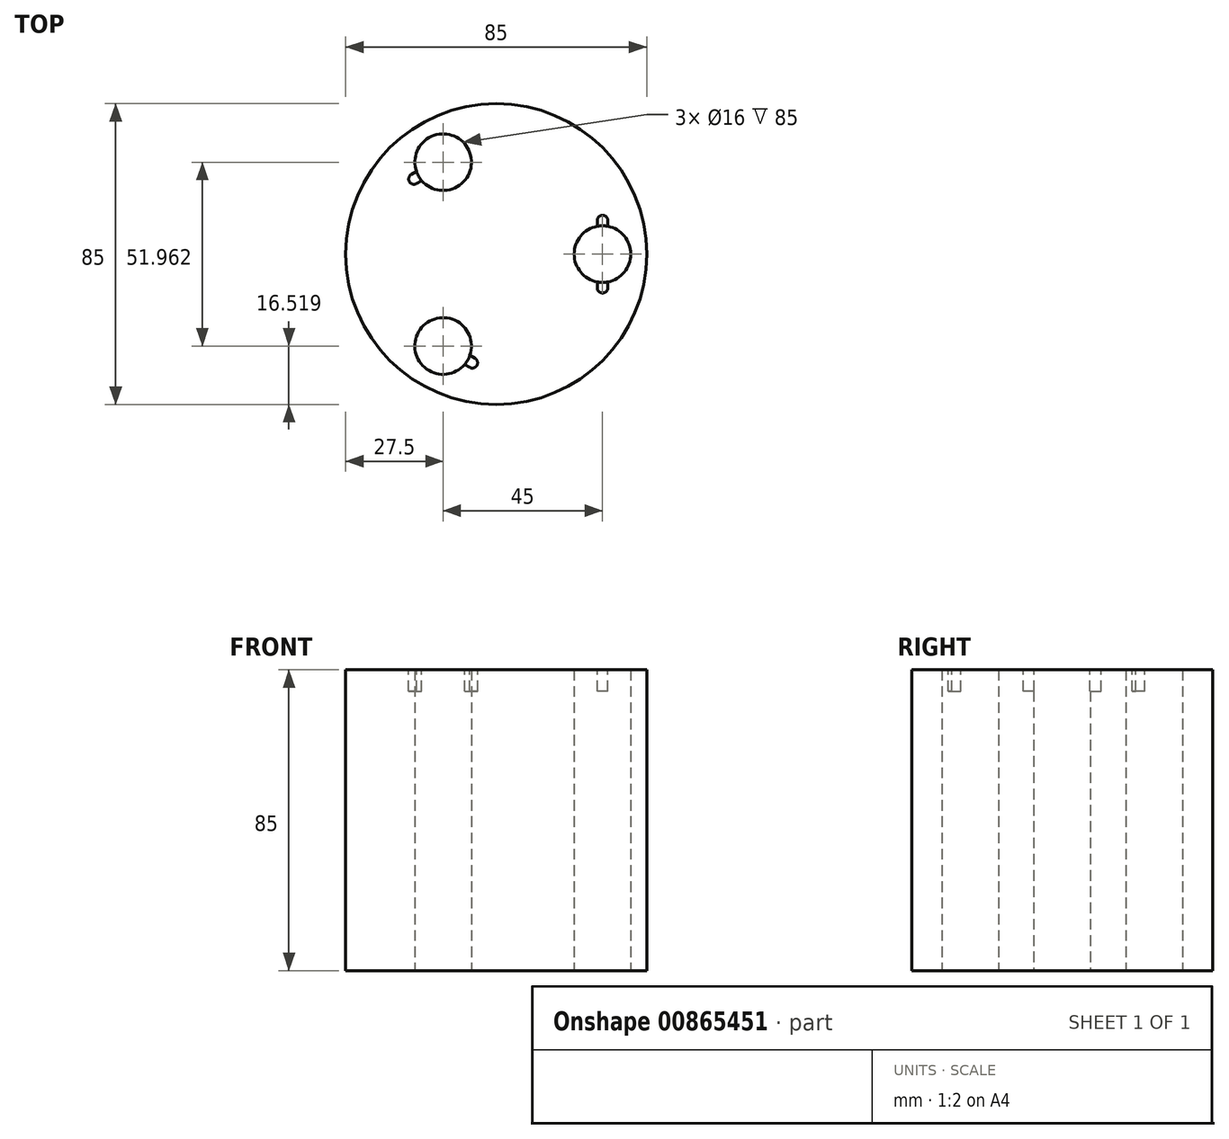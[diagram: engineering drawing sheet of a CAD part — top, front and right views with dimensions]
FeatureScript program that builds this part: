
annotation { "Feature Type Name" : "Feature", "Feature Type Description" : "" }
export const myFeature = defineFeature(function(context is Context, id is Id, definition is map)
    precondition{}
    {
        {
            var Q0;
            Q0=qCreatedBy(makeId("Top.planeOp"),FACE);
            var sketch = newSketch(context, id + "F0", { "sketchPlane" : qUnion([Q0])});
            skCircle(sketch, "E0", {"center": v(0, 0) * mm, "radius": 42.5 * mm});
            skCircle(sketch, "E1", {"center": v(30, 0) * mm, "radius": 8 * mm});
            skCircle(sketch, "E2.1.0", {"center": v(-15, 25.98) * mm, "radius": 8 * mm});
            skCircle(sketch, "E2.2.0", {"center": v(-15, -25.98) * mm, "radius": 8 * mm});
            skSolve(sketch);
        }
        {
            var Q0;
            Q0 = qSketchRegion(id + "F0", true);
            extrude(context, id + "F1", {"entities" : qUnion([Q0]), "depth" : 85 * mm, "offsetDistance" : 25 * mm});
        }
        {
            var Q0;
            Q0=makeQuery(id+"F1.opExtrude","CAP_FACE",FACE,{"disambiguationData":[OSD([sQuery(id+"F0.wireOp",EDGE,"E0"),sQuery(id+"F0.wireOp",EDGE,"E1"),sQuery(id+"F0.wireOp",EDGE,"E2.1.0"),sQuery(id+"F0.wireOp",EDGE,"E2.2.0")])],"isStart":false});
            var sketch = newSketch(context, id + "F2", { "sketchPlane" : qUnion([Q0])});
            skLineSegment(sketch, "E3", {"start": v(30, 0) * mm, "end": v(30, 11.66) * mm, "construction": true});
            skLineSegment(sketch, "E4", {"start": v(31.5, 7.86) * mm, "end": v(31.5, 9.5) * mm});
            skArc(sketch, "E5", {"start": v(31.5, 9.5) * mm, "mid": v(30, 11) * mm, "end": v(28.5, 9.5) * mm});
            skLineSegment(sketch, "E6", {"start": v(28.5, 9.5) * mm, "end": v(28.5, 7.86) * mm});
            skLineSegment(sketch, "E7", {"start": v(-59.08, 0) * mm, "end": v(58.12, 0) * mm, "construction": true});
            skLineSegment(sketch, "E8.MirrorCS", {"start": v(31.5, -7.86) * mm, "end": v(31.5, -9.5) * mm});
            skLineSegment(sketch, "E9.MirrorCS", {"start": v(28.5, -9.5) * mm, "end": v(28.5, -7.86) * mm});
            skArc(sketch, "E10.MirrorCS", {"start": v(31.5, -9.5) * mm, "mid": v(30, -11) * mm, "end": v(28.5, -9.5) * mm});
            skArc(sketch, "E11.1.0", {"start": v(-23.98, 22.53) * mm, "mid": v(-24.53, 20.48) * mm, "end": v(-22.48, 19.93) * mm});
            skLineSegment(sketch, "E11.1.1", {"start": v(-15, 25.98) * mm, "end": v(-25.1, 20.15) * mm, "construction": true});
            skArc(sketch, "E11.1.2", {"start": v(-7.52, 32.03) * mm, "mid": v(-5.47, 31.48) * mm, "end": v(-6.02, 29.43) * mm});
            skLineSegment(sketch, "E11.1.3", {"start": v(-8.94, 31.2) * mm, "end": v(-7.52, 32.03) * mm});
            skLineSegment(sketch, "E11.1.4", {"start": v(-22.48, 19.93) * mm, "end": v(-21.06, 20.75) * mm});
            skLineSegment(sketch, "E11.1.5", {"start": v(-22.56, 23.35) * mm, "end": v(-23.98, 22.53) * mm});
            skLineSegment(sketch, "E11.1.6", {"start": v(-6.02, 29.43) * mm, "end": v(-7.44, 28.61) * mm});
            skArc(sketch, "E11.2.0", {"start": v(-7.52, -32.03) * mm, "mid": v(-5.47, -31.48) * mm, "end": v(-6.02, -29.43) * mm});
            skLineSegment(sketch, "E11.2.1", {"start": v(-15, -25.98) * mm, "end": v(-4.9, -31.81) * mm, "construction": true});
            skArc(sketch, "E11.2.2", {"start": v(-23.98, -22.53) * mm, "mid": v(-24.53, -20.48) * mm, "end": v(-22.48, -19.93) * mm});
            skLineSegment(sketch, "E11.2.3", {"start": v(-22.56, -23.35) * mm, "end": v(-23.98, -22.53) * mm});
            skLineSegment(sketch, "E11.2.4", {"start": v(-6.02, -29.43) * mm, "end": v(-7.44, -28.61) * mm});
            skLineSegment(sketch, "E11.2.5", {"start": v(-8.94, -31.2) * mm, "end": v(-7.52, -32.03) * mm});
            skLineSegment(sketch, "E11.2.6", {"start": v(-22.48, -19.93) * mm, "end": v(-21.06, -20.75) * mm});
            skPoint(sketch, "E11.center", {"position": v(0, 0) * mm});
            skSolve(sketch);
        }
        {
            var Q0;
            {var subQ0=sQuery(id+"F2.wireOp",EDGE,"E4");Q0=makeQuery(id+"F2.imprint","IMPRINT",FACE,{"disambiguationData":[TD([[makeQuery(id+"F2.imprint","IMPRINT",EDGE,{"derivedFrom":subQ0}),1.0]])]});}
            var Q1;
            {var subQ0=sQuery(id+"F2.wireOp",EDGE,"E8.MirrorCS");Q1=makeQuery(id+"F2.imprint","IMPRINT",FACE,{"disambiguationData":[TD([[makeQuery(id+"F2.imprint","IMPRINT",EDGE,{"derivedFrom":subQ0}),-1.0]])]});}
            var Q2;
            Q2=makeQuery(id+"F2.imprint","IMPRINT",FACE,{"disambiguationData":[TD([[makeQuery(id+"F2.imprint","IMPRINT",EDGE,{"derivedFrom":sQuery(id+"F2.wireOp",EDGE,"E11.2.0")}),1.0]])]});
            var Q3;
            Q3=makeQuery(id+"F2.imprint","IMPRINT",FACE,{"disambiguationData":[TD([[makeQuery(id+"F2.imprint","IMPRINT",EDGE,{"derivedFrom":sQuery(id+"F2.wireOp",EDGE,"E11.2.2")}),-1.0]])]});
            var Q4;
            Q4=makeQuery(id+"F2.imprint","IMPRINT",FACE,{"disambiguationData":[TD([[makeQuery(id+"F2.imprint","IMPRINT",EDGE,{"derivedFrom":sQuery(id+"F2.wireOp",EDGE,"E11.1.0")}),1.0]])]});
            var Q5;
            Q5=makeQuery(id+"F2.imprint","IMPRINT",FACE,{"disambiguationData":[TD([[makeQuery(id+"F2.imprint","IMPRINT",EDGE,{"derivedFrom":sQuery(id+"F2.wireOp",EDGE,"E11.1.2")}),-1.0]])]});
            extrude(context, id + "F3", {"entities" : qUnion([Q0, Q1, Q2, Q3, Q4, Q5]), "operationType" : NewBodyOperationType.REMOVE, "oppositeDirection" : true, "depth" : (6) * mm, "offsetDistance" : 25 * mm});
        }
    });
